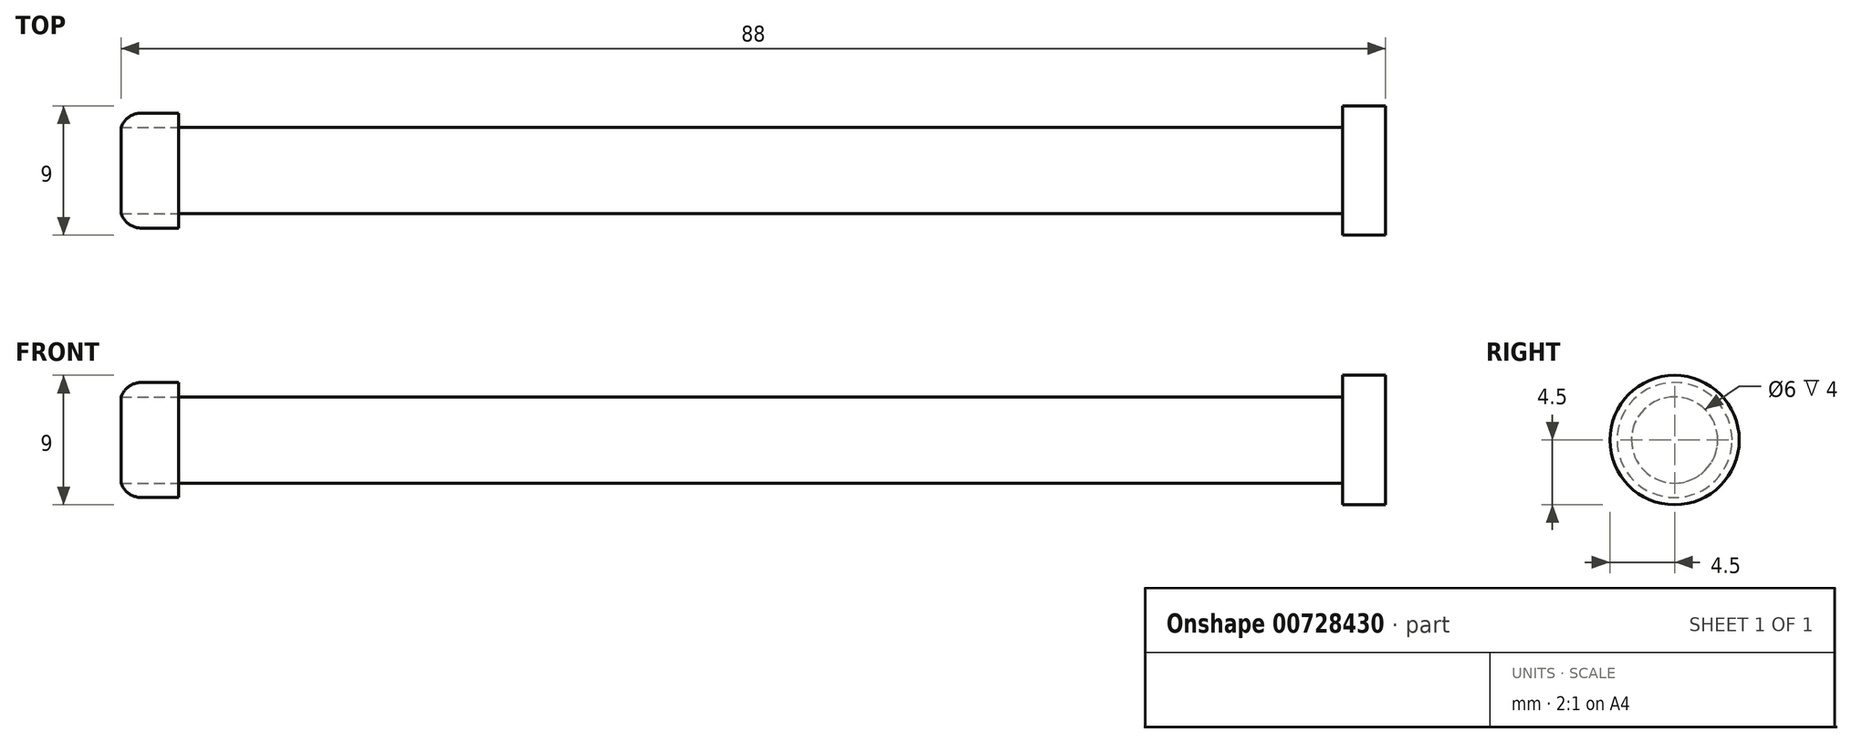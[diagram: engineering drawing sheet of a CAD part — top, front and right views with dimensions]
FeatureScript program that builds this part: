
annotation { "Feature Type Name" : "Feature", "Feature Type Description" : "" }
export const myFeature = defineFeature(function(context is Context, id is Id, definition is map)
    precondition{}
    {
        {
            var Q0;
            Q0=qCreatedBy(makeId("Top.planeOp"),FACE);
            var sketch = newSketch(context, id + "F0", { "sketchPlane" : qUnion([Q0])});
            skLineSegment(sketch, "E0.bottom", {"start": v(40.5, 3) * mm, "end": v(-40.5, 3) * mm});
            skLineSegment(sketch, "E0.top", {"start": v(40.5, -3) * mm, "end": v(-40.5, -3) * mm});
            skLineSegment(sketch, "E0.left", {"start": v(40.5, 3) * mm, "end": v(40.5, -3) * mm});
            skLineSegment(sketch, "E0.right", {"start": v(-40.5, 3) * mm, "end": v(-40.5, -3) * mm});
            skPoint(sketch, "E0.middle", {"position": v(0, 0) * mm});
            skSolve(sketch);
        }
        {
            var Q0;
            Q0=makeQuery(id+"F0.imprint","IMPRINT",FACE,{"disambiguationData":[TD([[makeQuery(id+"F0.imprint","IMPRINT",EDGE,{"derivedFrom":sQuery(id+"F0.wireOp",EDGE,"E0.bottom")}),1.0]])]});
            extrude(context, id + "F1", {"entities" : qUnion([Q0]), "endBound" : BoundingType.SYMMETRIC, "depth" : 6 * mm, "offsetDistance" : 25 * mm});
        }
        {
            var Q0;
            Q0=makeQuery(id+"F1.opExtrude","SWEPT_FACE",FACE,{"disambiguationData":[OSD([sQuery(id+"F0.wireOp",EDGE,"E0.left")])]});
            var sketch = newSketch(context, id + "F2", { "sketchPlane" : qUnion([Q0])});
            skLineSegment(sketch, "E1.bottom", {"start": v(4.5, 4.5) * mm, "end": v(-4.5, 4.5) * mm});
            skLineSegment(sketch, "E1.top", {"start": v(4.5, -4.5) * mm, "end": v(-4.5, -4.5) * mm});
            skLineSegment(sketch, "E1.left", {"start": v(4.5, 4.5) * mm, "end": v(4.5, -4.5) * mm});
            skPoint(sketch, "E1.middle", {"position": v(0, 0) * mm});
            skLineSegment(sketch, "E2", {"start": v(-4.5, 4.5) * mm, "end": v(-4.5, -4.5) * mm});
            skSolve(sketch);
        }
        {
            var Q0;
            Q0=makeQuery(id+"F1.opExtrude","CAP_EDGE",EDGE,{"disambiguationData":[OSD([sQuery(id+"F0.wireOp",EDGE,"E0.top")])],"isStart":false});
            var Q1;
            Q1=makeQuery(id+"F1.opExtrude","CAP_EDGE",EDGE,{"disambiguationData":[OSD([sQuery(id+"F0.wireOp",EDGE,"E0.top")])],"isStart":true});
            var Q2;
            Q2=makeQuery(id+"F1.opExtrude","CAP_EDGE",EDGE,{"disambiguationData":[OSD([sQuery(id+"F0.wireOp",EDGE,"E0.bottom")])],"isStart":false});
            var Q3;
            Q3=makeQuery(id+"F1.opExtrude","CAP_EDGE",EDGE,{"disambiguationData":[OSD([sQuery(id+"F0.wireOp",EDGE,"E0.bottom")])],"isStart":true});
            fillet(context, id + "F3", {"entities" : qUnion([Q0, Q1, Q2, Q3]), "radius" : 3 * mm, "tangentPropagation" : true, "allowEdgeOverflow" : false});
        }
        {
            var Q0;
            Q0=makeQuery(id+"F2.imprint","IMPRINT",FACE,{"disambiguationData":[TD([[makeQuery(id+"F2.imprint","IMPRINT",EDGE,{"derivedFrom":sQuery(id+"F2.wireOp",EDGE,"E1.bottom")}),1.0]])]});
            var Q1;
            {var subQ0=sQuery(id+"F0.wireOp",EDGE,"E0.left");Q1=makeQuery(id+"F2.imprint","IMPRINT",FACE,{"disambiguationData":[TD([[makeQuery(id+"F2.imprint","IMPRINT",EDGE,{"derivedFrom":makeQuery(id+"F1.opExtrude","CAP_EDGE",EDGE,{"disambiguationData":[OSD([subQ0])],"isStart":true})}),-1.0]])]});}
            extrude(context, id + "F4", {"entities" : qUnion([Q0, Q1]), "operationType" : NewBodyOperationType.ADD, "depth" : 3 * mm, "offsetDistance" : 25 * mm});
        }
        {
            var Q0;
            Q0=makeQuery(id+"F4.opExtrude","SWEPT_EDGE",EDGE,{"disambiguationData":[OSD([sQuery(id+"F2.wireOp",EDGE,"E1.bottom"),sQuery(id+"F2.wireOp",EDGE,"E1.left")])]});
            var Q1;
            Q1=makeQuery(id+"F4.opExtrude","SWEPT_EDGE",EDGE,{"disambiguationData":[OSD([sQuery(id+"F2.wireOp",EDGE,"E1.bottom"),sQuery(id+"F2.wireOp",EDGE,"E2")])]});
            var Q2;
            Q2=makeQuery(id+"F4.opExtrude","SWEPT_EDGE",EDGE,{"disambiguationData":[OSD([sQuery(id+"F2.wireOp",EDGE,"E1.top"),sQuery(id+"F2.wireOp",EDGE,"E2")])]});
            var Q3;
            Q3=makeQuery(id+"F4.opExtrude","SWEPT_EDGE",EDGE,{"disambiguationData":[OSD([sQuery(id+"F2.wireOp",EDGE,"E1.top"),sQuery(id+"F2.wireOp",EDGE,"E1.left")])]});
            fillet(context, id + "F5", {"entities" : qUnion([Q0, Q1, Q2, Q3]), "radius" : 4.5 * mm, "tangentPropagation" : true, "allowEdgeOverflow" : false});
        }
        {
            var Q0;
            Q0=makeQuery(id+"F1.opExtrude","SWEPT_FACE",FACE,{"disambiguationData":[OSD([sQuery(id+"F0.wireOp",EDGE,"E0.right")])]});
            var sketch = newSketch(context, id + "F6", { "sketchPlane" : qUnion([Q0])});
            skCircle(sketch, "E3", {"center": v(0, 0) * mm, "radius": 4 * mm});
            skSolve(sketch);
        }
        {
            var Q0;
            Q0=makeQuery(id+"F6.imprint","IMPRINT",FACE,{"disambiguationData":[TD([[makeQuery(id+"F6.imprint","IMPRINT",EDGE,{"derivedFrom":makeQuery(id+"F3.opFillet","BLEND_EDGE",EDGE,{"blendedFrom":[makeQuery(id+"F1.opExtrude","CAP_EDGE",EDGE,{"disambiguationData":[OSD([sQuery(id+"F0.wireOp",EDGE,"E0.top")])],"isStart":false}),makeQuery(id+"F1.opExtrude","SWEPT_FACE",FACE,{"disambiguationData":[OSD([sQuery(id+"F0.wireOp",EDGE,"E0.right")])]})],"blendedInto":[makeQuery(id+"F1.opExtrude","SWEPT_FACE",FACE,{"disambiguationData":[OSD([sQuery(id+"F0.wireOp",EDGE,"E0.right")])]})]})}),1.0]])]});
            var Q1;
            Q1=makeQuery(id+"F6.imprint","IMPRINT",FACE,{"disambiguationData":[TD([[makeQuery(id+"F6.imprint","IMPRINT",EDGE,{"derivedFrom":sQuery(id+"F6.wireOp",EDGE,"E3")}),1.0]])]});
            extrude(context, id + "F7", {"entities" : qUnion([Q0, Q1]), "operationType" : NewBodyOperationType.ADD, "depth" : 4 * mm, "offsetDistance" : 25 * mm});
        }
        {
            var Q0;
            Q0=makeQuery(id+"F7.opExtrude","CAP_EDGE",EDGE,{"disambiguationData":[OSD([sQuery(id+"F6.wireOp",EDGE,"E3")])],"isStart":false});
            fillet(context, id + "F8", {"entities" : qUnion([Q0]), "radius" : 1.5 * mm, "tangentPropagation" : true, "allowEdgeOverflow" : false});
        }
    });
